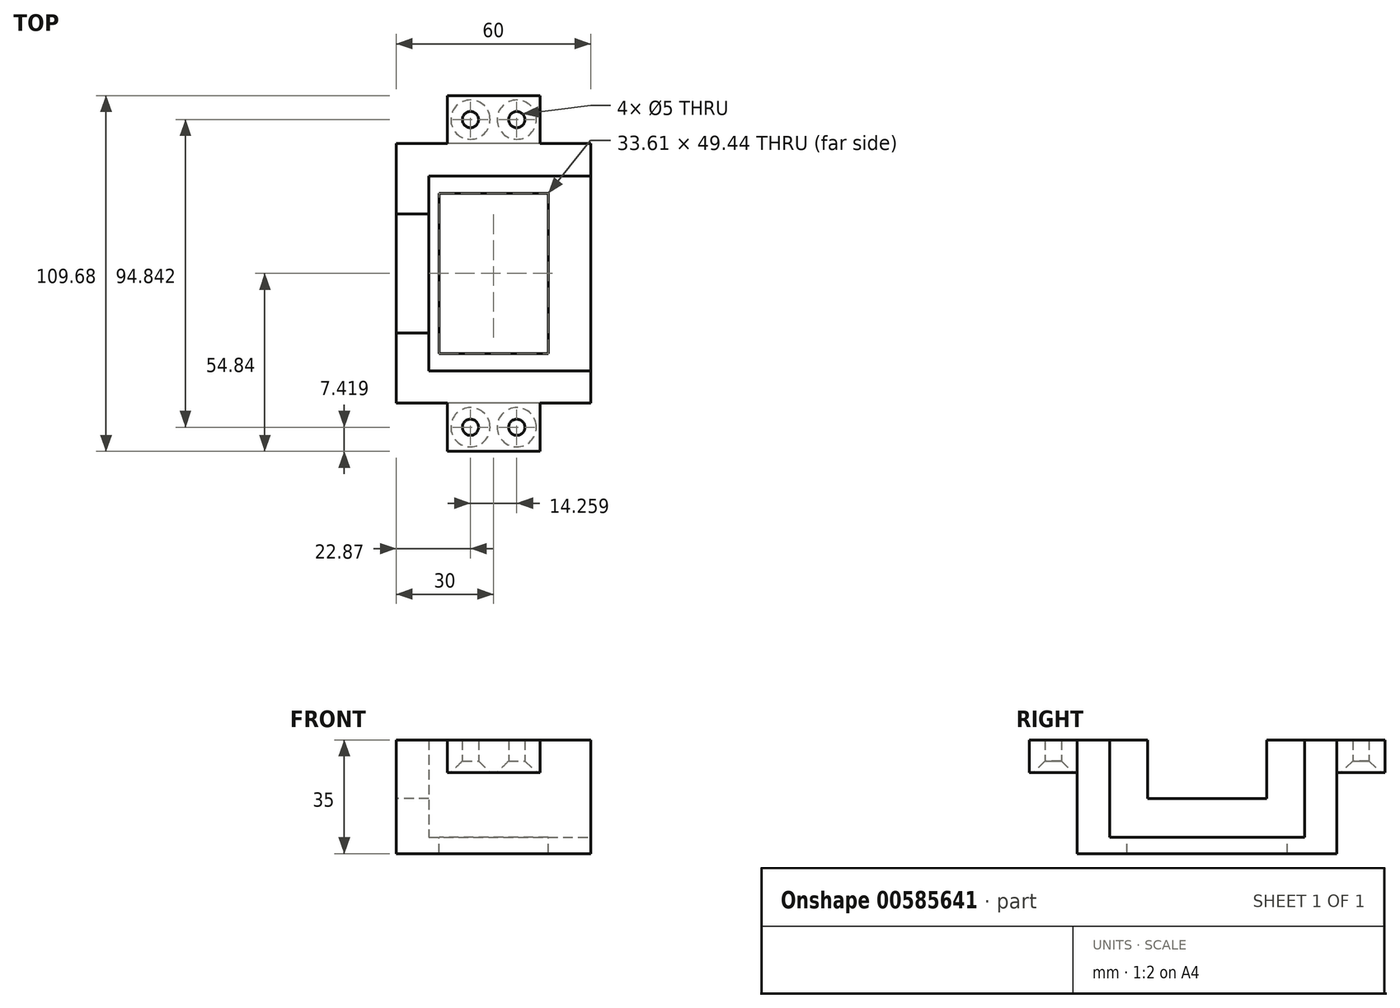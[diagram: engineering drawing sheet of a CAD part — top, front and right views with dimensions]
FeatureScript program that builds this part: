
annotation { "Feature Type Name" : "Feature", "Feature Type Description" : "" }
export const myFeature = defineFeature(function(context is Context, id is Id, definition is map)
    precondition{}
    {
        {
            var Q0;
            Q0=qCreatedBy(makeId("Top.planeOp"),FACE);
            var sketch = newSketch(context, id + "F0", { "sketchPlane" : qUnion([Q0])});
            skLineSegment(sketch, "E0.bottom", {"start": v(20, 30) * mm, "end": v(-20, 30) * mm});
            skLineSegment(sketch, "E0.top", {"start": v(20, -30) * mm, "end": v(-20, -30) * mm});
            skLineSegment(sketch, "E0.right", {"start": v(-20, 30) * mm, "end": v(-20, -30) * mm});
            skPoint(sketch, "E0.middle", {"position": v(0, 0) * mm});
            skLineSegment(sketch, "E1.bottom", {"start": v(30, 40) * mm, "end": v(-30, 40) * mm});
            skLineSegment(sketch, "E1.top", {"start": v(30, -40) * mm, "end": v(-30, -40) * mm});
            skLineSegment(sketch, "E1.left", {"start": v(30, 40) * mm, "end": v(30, -40) * mm});
            skLineSegment(sketch, "E1.right", {"start": v(-30, 40) * mm, "end": v(-30, -40) * mm});
            skLineSegment(sketch, "E2", {"start": v(20, 30) * mm, "end": v(30, 30) * mm});
            skLineSegment(sketch, "E3", {"start": v(20, -30) * mm, "end": v(30, -30) * mm});
            skSolve(sketch);
        }
        {
            var Q0;
            Q0=makeQuery(id+"F0.imprint","IMPRINT",FACE,{"disambiguationData":[TD([[makeQuery(id+"F0.imprint","IMPRINT",EDGE,{"derivedFrom":sQuery(id+"F0.wireOp",EDGE,"E0.bottom")}),-1.0]])]});
            extrude(context, id + "F1", {"entities" : qUnion([Q0]), "depth" : 35 * mm, "offsetDistance" : 25 * mm});
        }
        {
            var Q0;
            Q0=makeQuery(id+"F0.imprint","IMPRINT",FACE,{"disambiguationData":[TD([[makeQuery(id+"F0.imprint","IMPRINT",EDGE,{"derivedFrom":sQuery(id+"F0.wireOp",EDGE,"E0.bottom")}),1.0]])]});
            extrude(context, id + "F2", {"entities" : qUnion([Q0]), "operationType" : NewBodyOperationType.ADD, "depth" : 5 * mm, "offsetDistance" : 25 * mm});
        }
        {
            var Q0;
            Q0=makeQuery(id+"F2.opExtrude","CAP_FACE",FACE,{"disambiguationData":[OSD([sQuery(id+"F0.wireOp",EDGE,"E0.bottom"),sQuery(id+"F0.wireOp",EDGE,"E0.top"),sQuery(id+"F0.wireOp",EDGE,"E0.right"),sQuery(id+"F0.wireOp",EDGE,"E1.left"),sQuery(id+"F0.wireOp",EDGE,"E2"),sQuery(id+"F0.wireOp",EDGE,"E3")])],"isStart":false});
            var sketch = newSketch(context, id + "F3", { "sketchPlane" : qUnion([Q0])});
            skLineSegment(sketch, "E4.bottom", {"start": v(16.8, 24.72) * mm, "end": v(-16.8, 24.72) * mm});
            skLineSegment(sketch, "E4.top", {"start": v(16.8, -24.72) * mm, "end": v(-16.8, -24.72) * mm});
            skLineSegment(sketch, "E4.left", {"start": v(16.8, 24.72) * mm, "end": v(16.8, -24.72) * mm});
            skLineSegment(sketch, "E4.right", {"start": v(-16.8, 24.72) * mm, "end": v(-16.8, -24.72) * mm});
            skPoint(sketch, "E4.middle", {"position": v(0, 0) * mm});
            skSolve(sketch);
        }
        {
            var Q0;
            Q0=makeQuery(id+"F3.imprint","IMPRINT",FACE,{"disambiguationData":[TD([[makeQuery(id+"F3.imprint","IMPRINT",EDGE,{"derivedFrom":sQuery(id+"F3.wireOp",EDGE,"E4.bottom")}),1.0]])]});
            extrude(context, id + "F4", {"entities" : qUnion([Q0]), "operationType" : NewBodyOperationType.REMOVE, "oppositeDirection" : true, "depth" : 25 * mm, "offsetDistance" : 25 * mm});
        }
        {
            var Q0;
            Q0=makeQuery(id+"F1.opExtrude","CAP_FACE",FACE,{"disambiguationData":[OSD([sQuery(id+"F0.wireOp",EDGE,"E0.bottom"),sQuery(id+"F0.wireOp",EDGE,"E0.top"),sQuery(id+"F0.wireOp",EDGE,"E0.right"),sQuery(id+"F0.wireOp",EDGE,"E1.bottom"),sQuery(id+"F0.wireOp",EDGE,"E1.top"),sQuery(id+"F0.wireOp",EDGE,"E1.left"),sQuery(id+"F0.wireOp",EDGE,"E1.right"),sQuery(id+"F0.wireOp",EDGE,"E2"),sQuery(id+"F0.wireOp",EDGE,"E3")])],"isStart":false});
            var sketch = newSketch(context, id + "F5", { "sketchPlane" : qUnion([Q0])});
            skLineSegment(sketch, "E5.bottom", {"start": v(14.26, 54.84) * mm, "end": v(-14.26, 54.84) * mm});
            skLineSegment(sketch, "E5.top", {"start": v(14.26, -54.84) * mm, "end": v(-14.26, -54.84) * mm});
            skLineSegment(sketch, "E5.left", {"start": v(14.26, 54.84) * mm, "end": v(14.26, 30) * mm});
            skLineSegment(sketch, "E5.right", {"start": v(-14.26, 54.84) * mm, "end": v(-14.26, -30.05) * mm});
            skPoint(sketch, "E5.middle", {"position": v(0, 0) * mm});
            skLineSegment(sketch, "E6", {"start": v(-14.26, -40) * mm, "end": v(14.26, -40) * mm});
            skLineSegment(sketch, "E7", {"start": v(14.26, -40) * mm, "end": v(14.26, 30) * mm});
            skLineSegment(sketch, "E8", {"start": v(-14.26, 30) * mm, "end": v(-14.26, 30) * mm});
            skPoint(sketch, "E9", {"position": v(-14.26, 30) * mm});
            skPoint(sketch, "E10", {"position": v(14.26, 30) * mm});
            skLineSegment(sketch, "E11", {"start": v(-14.26, 30) * mm, "end": v(14.26, 30) * mm});
            skLineSegment(sketch, "E12", {"start": v(14.26, 30) * mm, "end": v(14.26, -30.27) * mm});
            skLineSegment(sketch, "E13", {"start": v(-14.26, -30.05) * mm, "end": v(-14.26, -54.84) * mm});
            skLineSegment(sketch, "E14", {"start": v(14.26, -30.27) * mm, "end": v(14.26, -54.84) * mm});
            skSolve(sketch);
        }
        {
            var Q0;
            {var subQ0=sQuery(id+"F5.wireOp",EDGE,"E5.top");Q0=makeQuery(id+"F5.imprint","IMPRINT",FACE,{"disambiguationData":[TD([[makeQuery(id+"F5.imprint","IMPRINT",EDGE,{"derivedFrom":subQ0}),-1.0]])]});}
            var Q1;
            {var subQ0=sQuery(id+"F5.wireOp",EDGE,"E5.bottom");Q1=makeQuery(id+"F5.imprint","IMPRINT",FACE,{"disambiguationData":[TD([[makeQuery(id+"F5.imprint","IMPRINT",EDGE,{"derivedFrom":subQ0}),1.0]])]});}
            extrude(context, id + "F6", {"entities" : qUnion([Q0, Q1]), "operationType" : NewBodyOperationType.ADD, "oppositeDirection" : true, "depth" : 10 * mm, "offsetDistance" : 25 * mm});
        }
        {
            var Q0;
            Q0=makeQuery(id+"F6.opExtrude","CAP_FACE",FACE,{"disambiguationData":[OSD([sQuery(id+"F5.wireOp",EDGE,"E5.top"),sQuery(id+"F5.wireOp",EDGE,"E6"),sQuery(id+"F5.wireOp",EDGE,"E13"),sQuery(id+"F5.wireOp",EDGE,"E14")])],"isStart":false});
            var sketch = newSketch(context, id + "F7", { "sketchPlane" : qUnion([Q0])});
            skLineSegment(sketch, "E15.bottom", {"start": v(14.26, 54.84) * mm, "end": v(-14.26, 54.84) * mm});
            skLineSegment(sketch, "E15.top", {"start": v(14.26, 47.42) * mm, "end": v(7.13, 47.42) * mm});
            skLineSegment(sketch, "E15.left", {"start": v(14.26, 54.84) * mm, "end": v(14.26, 47.42) * mm});
            skLineSegment(sketch, "E15.right", {"start": v(-14.26, 54.84) * mm, "end": v(-14.26, 47.42) * mm});
            skLineSegment(sketch, "E16.bottom", {"start": v(-14.26, 54.84) * mm, "end": v(-14.26, 54.84) * mm});
            skLineSegment(sketch, "E16.top", {"start": v(-14.26, 47.42) * mm, "end": v(-14.26, 47.42) * mm});
            skLineSegment(sketch, "E17.left", {"start": v(-14.26, 47.42) * mm, "end": v(-14.26, 54.84) * mm});
            skLineSegment(sketch, "E17.right", {"start": v(-14.26, 47.42) * mm, "end": v(-14.26, 54.84) * mm});
            skLineSegment(sketch, "E18", {"start": v(0, 47.42) * mm, "end": v(-7.13, 47.42) * mm});
            skLineSegment(sketch, "E19", {"start": v(0, 54.84) * mm, "end": v(0, 40.7) * mm});
            skLineSegment(sketch, "E20", {"start": v(7.13, 47.42) * mm, "end": v(0, 47.42) * mm});
            skLineSegment(sketch, "E21", {"start": v(-7.13, 47.42) * mm, "end": v(-14.26, 47.42) * mm});
            skSolve(sketch);
        }
        {
            var Q0;
            Q0=makeQuery(id+"F6.opExtrude","CAP_FACE",FACE,{"disambiguationData":[OSD([sQuery(id+"F0.wireOp",EDGE,"E1.bottom"),sQuery(id+"F5.wireOp",EDGE,"E5.bottom"),sQuery(id+"F5.wireOp",EDGE,"E5.left"),sQuery(id+"F5.wireOp",EDGE,"E5.right")])],"isStart":false});
            var sketch = newSketch(context, id + "F8", { "sketchPlane" : qUnion([Q0])});
            skLineSegment(sketch, "E22.bottom", {"start": v(14.26, -54.84) * mm, "end": v(-14.26, -54.84) * mm});
            skLineSegment(sketch, "E22.top", {"start": v(14.26, -47.42) * mm, "end": v(7.13, -47.42) * mm});
            skLineSegment(sketch, "E22.left", {"start": v(14.26, -54.84) * mm, "end": v(14.26, -47.42) * mm});
            skLineSegment(sketch, "E22.right", {"start": v(-14.26, -54.84) * mm, "end": v(-14.26, -47.42) * mm});
            skLineSegment(sketch, "E23", {"start": v(0, -47.42) * mm, "end": v(-7.13, -47.42) * mm});
            skLineSegment(sketch, "E24", {"start": v(7.13, -47.42) * mm, "end": v(0, -47.42) * mm});
            skLineSegment(sketch, "E25", {"start": v(-7.13, -47.42) * mm, "end": v(-14.26, -47.42) * mm});
            skSolve(sketch);
        }
        {
            var Q0;
            Q0=sQuery(id+"F7.wireOp",VERTEX,"E20.start");
            var Q1;
            Q1=sQuery(id+"F7.wireOp",VERTEX,"E21.start");
            var Q2;
            Q2=sQuery(id+"F8.wireOp",VERTEX,"E25.start");
            var Q3;
            Q3=sQuery(id+"F8.wireOp",VERTEX,"E24.start");
            var Q4;
            Q4=makeQuery(id+"F1.opExtrude","SWEPT_BODY",BODY,{"disambiguationData":[OSD([sQuery(id+"F0.wireOp",EDGE,"E0.bottom"),sQuery(id+"F0.wireOp",EDGE,"E0.top"),sQuery(id+"F0.wireOp",EDGE,"E0.right"),sQuery(id+"F0.wireOp",EDGE,"E1.bottom"),sQuery(id+"F0.wireOp",EDGE,"E1.top"),sQuery(id+"F0.wireOp",EDGE,"E1.left"),sQuery(id+"F0.wireOp",EDGE,"E1.right"),sQuery(id+"F0.wireOp",EDGE,"E2"),sQuery(id+"F0.wireOp",EDGE,"E3")])]});
            hole(context, id + "F9", {"style" : HoleStyle.C_SINK, "endStyle" : HoleEndStyle.THROUGH, "holeDiameter" : 5 * mm, "cSinkDiameter" : 12.1 * mm, "cSinkAngle" : 90 * degree, "majorDiameter" : 5 * mm, "isTappedThrough" : true, "tappedDepth" : 12 * mm, "tapClearance" : 3, "locations" : qUnion([Q0, Q1, Q2, Q3]), "scope" : qUnion([Q4])});
        }
        {
            var Q0;
            Q0=makeQuery(id+"F1.opExtrude","SWEPT_FACE",FACE,{"disambiguationData":[OSD([sQuery(id+"F0.wireOp",EDGE,"E1.right")])]});
            var sketch = newSketch(context, id + "F10", { "sketchPlane" : qUnion([Q0])});
            skLineSegment(sketch, "E26.bottom", {"start": v(-18.39, 16.99) * mm, "end": v(18.39, 16.99) * mm});
            skLineSegment(sketch, "E26.top", {"start": v(-18.39, 53.01) * mm, "end": v(18.39, 53.01) * mm});
            skLineSegment(sketch, "E26.left", {"start": v(-18.39, 16.99) * mm, "end": v(-18.39, 53.01) * mm});
            skLineSegment(sketch, "E26.right", {"start": v(18.39, 16.99) * mm, "end": v(18.39, 53.01) * mm});
            skPoint(sketch, "E26.middle", {"position": v(0, 35) * mm});
            skSolve(sketch);
        }
        {
            var Q0;
            Q0 = qSketchRegion(id + "F10", true);
            extrude(context, id + "F11", {"entities" : qUnion([Q0]), "operationType" : NewBodyOperationType.REMOVE, "oppositeDirection" : true, "depth" : 25 * mm, "offsetDistance" : 25 * mm});
        }
    });
